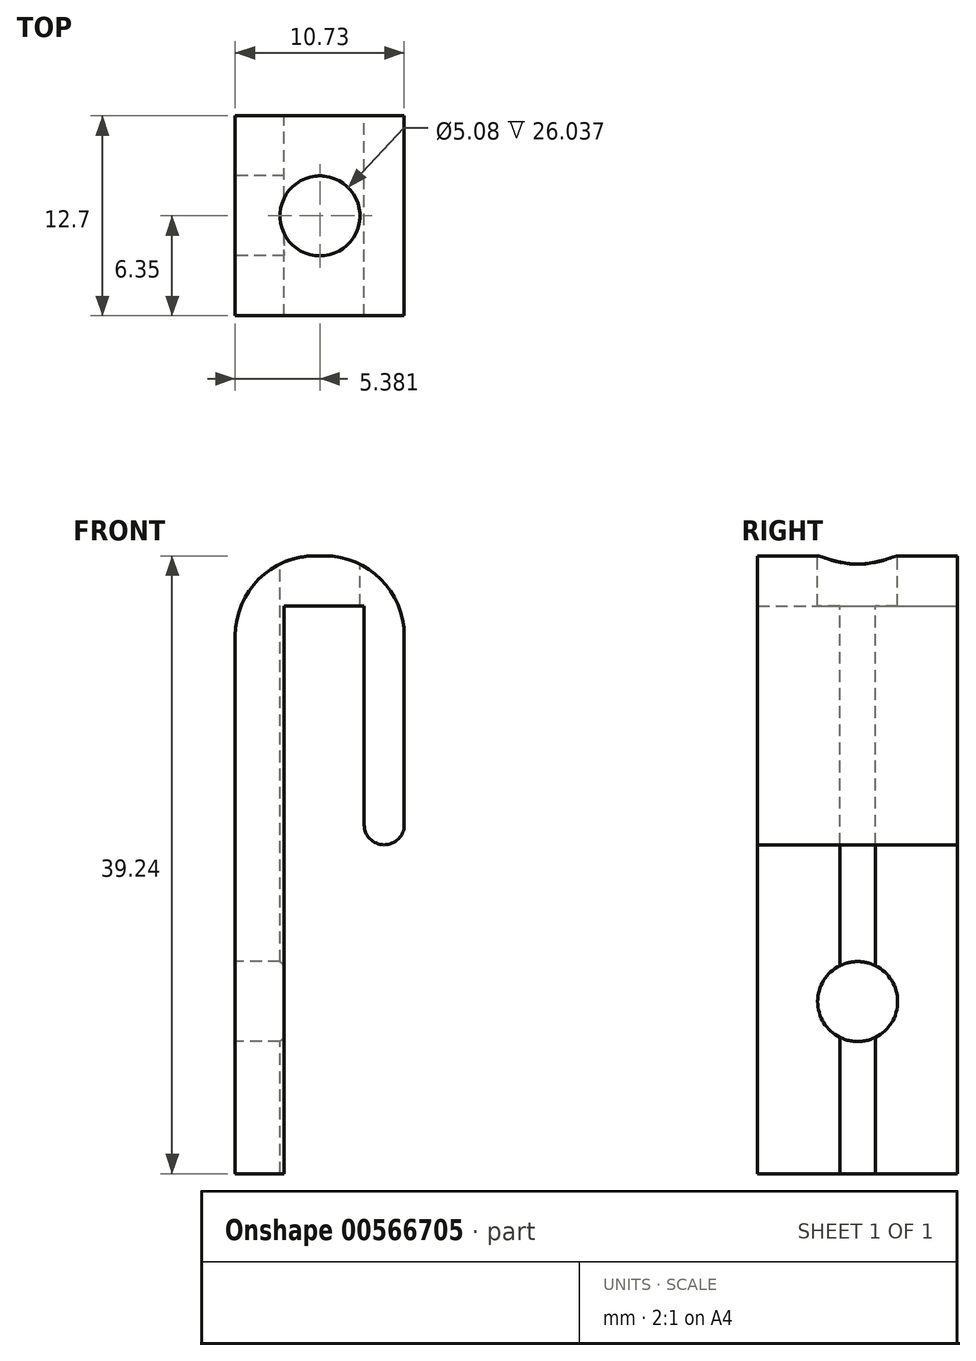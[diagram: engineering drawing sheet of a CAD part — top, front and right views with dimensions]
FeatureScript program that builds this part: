
annotation { "Feature Type Name" : "Feature", "Feature Type Description" : "" }
export const myFeature = defineFeature(function(context is Context, id is Id, definition is map)
    precondition{}
    {
        {
            var Q0;
            Q0=qCreatedBy(makeId("Front.planeOp"),FACE);
            var sketch = newSketch(context, id + "F0", { "sketchPlane" : qUnion([Q0])});
            skLineSegment(sketch, "E0", {"start": v(0, 0) * mm, "end": v(0, 18.35) * mm});
            skLineSegment(sketch, "E1", {"start": v(0, 18.35) * mm, "end": v(-10.73, 18.35) * mm});
            skLineSegment(sketch, "E2", {"start": v(-10.73, 18.35) * mm, "end": v(-10.73, -20.9) * mm});
            skLineSegment(sketch, "E3", {"start": v(-10.73, -20.9) * mm, "end": v(-7.62, -20.9) * mm});
            skLineSegment(sketch, "E4", {"start": v(-7.62, -20.9) * mm, "end": v(-7.62, 15.18) * mm});
            skLineSegment(sketch, "E5", {"start": v(-7.62, 15.18) * mm, "end": v(-2.54, 15.18) * mm});
            skLineSegment(sketch, "E6", {"start": v(-2.54, 15.18) * mm, "end": v(-2.54, 0) * mm});
            skLineSegment(sketch, "E7", {"start": v(-2.54, 0) * mm, "end": v(0, 0) * mm});
            skPoint(sketch, "E8", {"position": v(-10.73, -1.27) * mm});
            skPoint(sketch, "E9", {"position": v(-5.08, 18.35) * mm});
            skPoint(sketch, "E9.positionSnap0", {"position": v(-5.08, 15.18) * mm});
            skSolve(sketch);
        }
        {
            var Q0;
            Q0=makeQuery(id+"F0.imprint","IMPRINT",FACE,{"disambiguationData":[TD([[makeQuery(id+"F0.imprint","IMPRINT",EDGE,{"derivedFrom":sQuery(id+"F0.wireOp",EDGE,"E0")}),1.0]])]});
            extrude(context, id + "F1", {"entities" : qUnion([Q0]), "endBound" : BoundingType.SYMMETRIC, "depth" : 12.7 * mm, "offsetDistance" : 25.4 * mm});
        }
        {
            var Q0;
            Q0=makeQuery(id+"F1.opExtrude","SWEPT_EDGE",EDGE,{"disambiguationData":[OSD([sQuery(id+"F0.wireOp",EDGE,"E0"),sQuery(id+"F0.wireOp",EDGE,"E1")])]});
            var Q1;
            Q1=makeQuery(id+"F1.opExtrude","SWEPT_EDGE",EDGE,{"disambiguationData":[OSD([sQuery(id+"F0.wireOp",EDGE,"E1"),sQuery(id+"F0.wireOp",EDGE,"E2")])]});
            fillet(context, id + "F2", {"entities" : qUnion([Q0, Q1]), "radius" : 5.08 * mm, "tangentPropagation" : true, "allowEdgeOverflow" : false});
        }
        {
            var Q0;
            Q0=makeQuery(id+"F1.opExtrude","SWEPT_FACE",FACE,{"disambiguationData":[OSD([sQuery(id+"F0.wireOp",EDGE,"E2")])]});
            var sketch = newSketch(context, id + "F3", { "sketchPlane" : qUnion([Q0])});
            skCircle(sketch, "E10", {"center": v(0, -9.96) * mm, "radius": 2.46 * mm});
            skSolve(sketch);
        }
        {
            var Q0;
            Q0=makeQuery(id+"F1.opExtrude","SWEPT_FACE",FACE,{"disambiguationData":[OSD([sQuery(id+"F0.wireOp",EDGE,"E1")])]});
            var sketch = newSketch(context, id + "F4", { "sketchPlane" : qUnion([Q0])});
            skCircle(sketch, "E11", {"center": v(-5.35, 0) * mm, "radius": 1.18 * mm});
            skPoint(sketch, "E11.centerSnap0", {"position": v(-5.65, 0) * mm});
            skSolve(sketch);
        }
        {
            var Q0;
            Q0=sQuery(id+"F4.wireOp",VERTEX,"E11.center");
            var Q1;
            Q1=makeQuery(id+"F1.opExtrude","SWEPT_BODY",BODY,{"disambiguationData":[OSD([sQuery(id+"F0.wireOp",EDGE,"E0"),sQuery(id+"F0.wireOp",EDGE,"E1"),sQuery(id+"F0.wireOp",EDGE,"E2"),sQuery(id+"F0.wireOp",EDGE,"E3"),sQuery(id+"F0.wireOp",EDGE,"E4"),sQuery(id+"F0.wireOp",EDGE,"E5"),sQuery(id+"F0.wireOp",EDGE,"E6"),sQuery(id+"F0.wireOp",EDGE,"E7")])]});
            hole(context, id + "F5", {"style" : HoleStyle.SIMPLE, "endStyle" : HoleEndStyle.THROUGH, "holeDiameter" : 5.08 * mm, "isTappedThrough" : true, "tappedDepth" : 12.7 * mm, "tapClearance" : 3, "locations" : qUnion([Q0]), "scope" : qUnion([Q1])});
        }
        {
            var Q0;
            Q0=sQuery(id+"F3.wireOp",VERTEX,"E10.center");
            var Q1;
            Q1=makeQuery(id+"F1.opExtrude","SWEPT_BODY",BODY,{"disambiguationData":[OSD([sQuery(id+"F0.wireOp",EDGE,"E0"),sQuery(id+"F0.wireOp",EDGE,"E1"),sQuery(id+"F0.wireOp",EDGE,"E2"),sQuery(id+"F0.wireOp",EDGE,"E3"),sQuery(id+"F0.wireOp",EDGE,"E4"),sQuery(id+"F0.wireOp",EDGE,"E5"),sQuery(id+"F0.wireOp",EDGE,"E6"),sQuery(id+"F0.wireOp",EDGE,"E7")])]});
            hole(context, id + "F6", {"style" : HoleStyle.SIMPLE, "endStyle" : HoleEndStyle.THROUGH, "holeDiameter" : 5.08 * mm, "isTappedThrough" : true, "tappedDepth" : 12.7 * mm, "tapClearance" : 3, "locations" : qUnion([Q0]), "scope" : qUnion([Q1])});
        }
        {
            var Q0;
            Q0=makeQuery(id+"F1.opExtrude","SWEPT_EDGE",EDGE,{"disambiguationData":[OSD([sQuery(id+"F0.wireOp",EDGE,"E0"),sQuery(id+"F0.wireOp",EDGE,"E7")])]});
            var Q1;
            Q1=makeQuery(id+"F1.opExtrude","SWEPT_EDGE",EDGE,{"disambiguationData":[OSD([sQuery(id+"F0.wireOp",EDGE,"E6"),sQuery(id+"F0.wireOp",EDGE,"E7")])]});
            fillet(context, id + "F7", {"entities" : qUnion([Q0, Q1]), "radius" : 1.27 * mm, "tangentPropagation" : true, "allowEdgeOverflow" : false});
        }
    });
